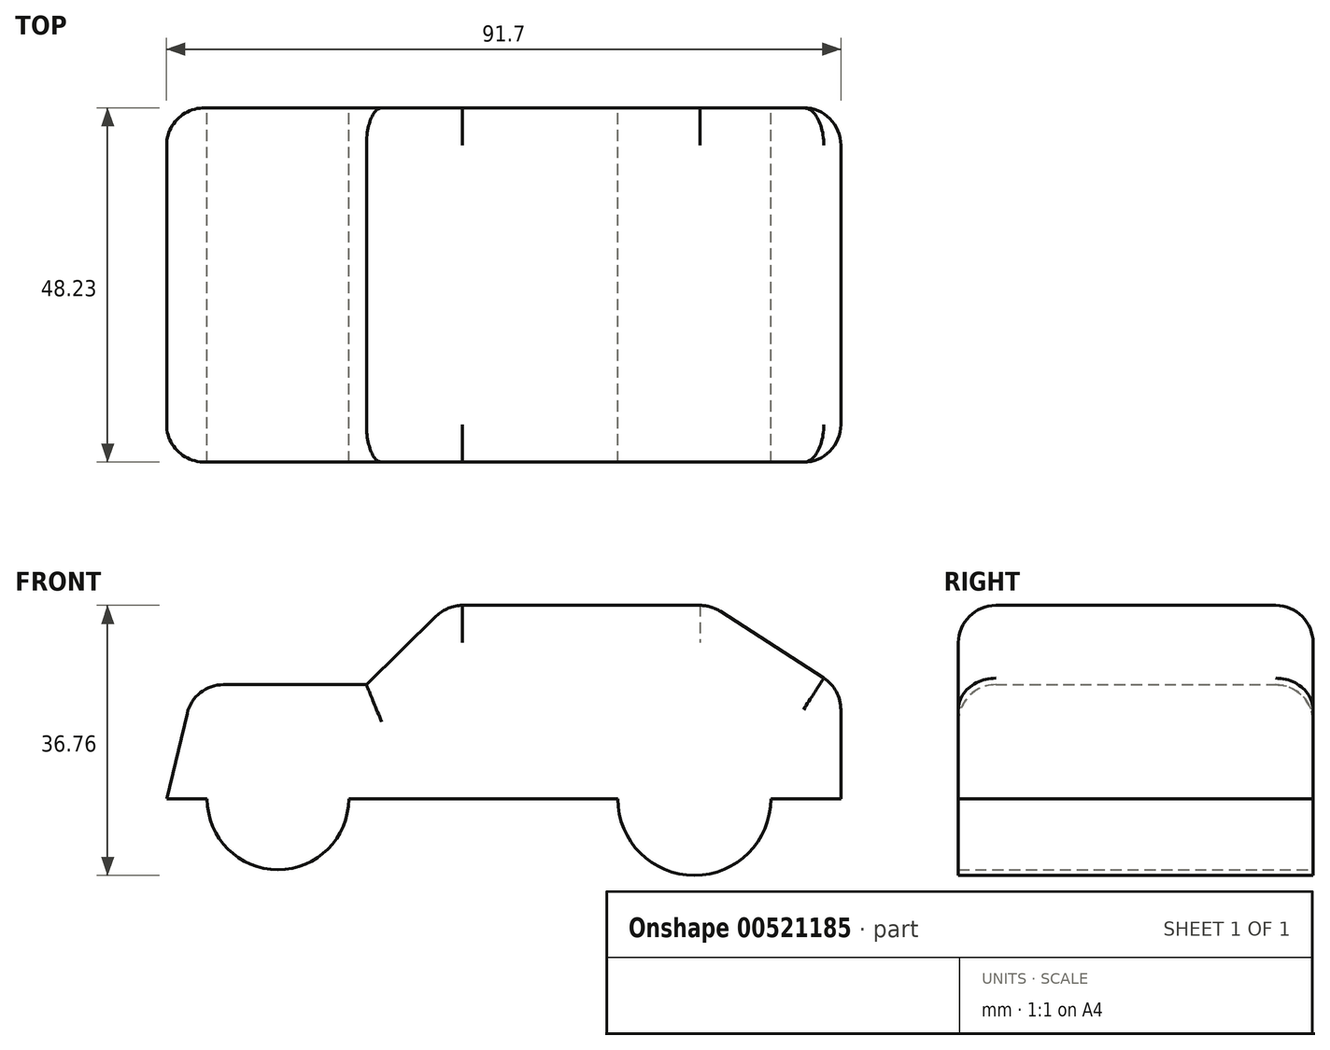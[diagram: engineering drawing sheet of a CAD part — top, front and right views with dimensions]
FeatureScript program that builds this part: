
annotation { "Feature Type Name" : "Feature", "Feature Type Description" : "" }
export const myFeature = defineFeature(function(context is Context, id is Id, definition is map)
    precondition{}
    {
        {
            var Q0;
            Q0=qCreatedBy(makeId("Front.planeOp"),FACE);
            var sketch = newSketch(context, id + "F0", { "sketchPlane" : qUnion([Q0])});
            skLineSegment(sketch, "E0", {"start": v(-48.55, 0) * mm, "end": v(43.15, 0) * mm});
            skLineSegment(sketch, "E1", {"start": v(43.15, 0) * mm, "end": v(43.15, 14.94) * mm});
            skLineSegment(sketch, "E2", {"start": v(43.15, 14.94) * mm, "end": v(25.52, 26.35) * mm});
            skLineSegment(sketch, "E3", {"start": v(25.52, 26.35) * mm, "end": v(-10.37, 26.35) * mm});
            skLineSegment(sketch, "E4", {"start": v(-10.37, 26.35) * mm, "end": v(-21.37, 15.56) * mm});
            skLineSegment(sketch, "E5", {"start": v(-21.37, 15.56) * mm, "end": v(-44.81, 15.56) * mm});
            skLineSegment(sketch, "E6", {"start": v(-44.81, 15.56) * mm, "end": v(-48.55, 0) * mm});
            skCircle(sketch, "E7", {"center": v(-33.4, 0) * mm, "radius": 9.62 * mm});
            skCircle(sketch, "E8", {"center": v(23.24, 0) * mm, "radius": 10.4 * mm});
            skSolve(sketch);
        }
        {
            var Q0;
            Q0 = qSketchRegion(id + "F0", true);
            extrude(context, id + "F1", {"entities" : qUnion([Q0]), "depth" : 25.4 * mm, "offsetDistance" : 25.4 * mm});
        }
        {
            var Q0;
            Q0=makeQuery(id+"F1.opExtrude","CAP_FACE",FACE,{"disambiguationData":[OSD([sQuery(id+"F0.wireOp",EDGE,"E0"),sQuery(id+"F0.wireOp",EDGE,"E1"),sQuery(id+"F0.wireOp",EDGE,"E2"),sQuery(id+"F0.wireOp",EDGE,"E3"),sQuery(id+"F0.wireOp",EDGE,"E4"),sQuery(id+"F0.wireOp",EDGE,"E5"),sQuery(id+"F0.wireOp",EDGE,"E6"),sQuery(id+"F0.wireOp",EDGE,"E7"),sQuery(id+"F0.wireOp",EDGE,"E8")])],"isStart":true});
            extrude(context, id + "F2", {"entities" : qUnion([Q0]), "operationType" : NewBodyOperationType.ADD, "depth" : 22.83 * mm, "offsetDistance" : 25.4 * mm});
        }
        {
            var Q0;
            Q0=makeQuery(id+"F2.opExtrude","CAP_EDGE",EDGE,{"disambiguationData":[OSD([sQuery(id+"F0.wireOp",EDGE,"E3")])],"isStart":false});
            fillet(context, id + "F3", {"entities" : qUnion([Q0]), "radius" : 5.08 * mm, "tangentPropagation" : true, "allowEdgeOverflow" : false});
        }
        {
            var Q0;
            Q0=makeQuery(id+"F2.opExtrude","CAP_EDGE",EDGE,{"disambiguationData":[OSD([sQuery(id+"F0.wireOp",EDGE,"E5")])],"isStart":false});
            fillet(context, id + "F4", {"entities" : qUnion([Q0]), "radius" : 5.08 * mm, "tangentPropagation" : true, "allowEdgeOverflow" : false});
        }
        {
            var Q0;
            Q0=makeQuery(id+"F2.opExtrude","CAP_EDGE",EDGE,{"disambiguationData":[OSD([sQuery(id+"F0.wireOp",EDGE,"E2")])],"isStart":false});
            fillet(context, id + "F5", {"entities" : qUnion([Q0]), "radius" : 5.08 * mm, "tangentPropagation" : true, "allowEdgeOverflow" : false});
        }
        {
            var Q0;
            Q0=makeQuery(id+"F1.opExtrude","CAP_EDGE",EDGE,{"disambiguationData":[OSD([sQuery(id+"F0.wireOp",EDGE,"E2")])],"isStart":false});
            fillet(context, id + "F6", {"entities" : qUnion([Q0]), "radius" : 5.08 * mm, "tangentPropagation" : true, "allowEdgeOverflow" : false});
        }
        {
            var Q0;
            Q0=makeQuery(id+"F1.opExtrude","CAP_EDGE",EDGE,{"disambiguationData":[OSD([sQuery(id+"F0.wireOp",EDGE,"E5")])],"isStart":false});
            fillet(context, id + "F7", {"entities" : qUnion([Q0]), "radius" : 5.08 * mm, "tangentPropagation" : true, "allowEdgeOverflow" : false});
        }
        {
            var Q0;
            {var subQ0=sQuery(id+"F0.wireOp",EDGE,"E4");Q0=makeQuery(id+"F3.opFillet","BLEND_EDGE",EDGE,{"blendedFrom":[makeQuery(id+"F2.opExtrude","CAP_EDGE",EDGE,{"disambiguationData":[OSD([sQuery(id+"F0.wireOp",EDGE,"E3")])],"isStart":false}),makeQuery(id+"F2.boolean.opBoolean","MERGE",FACE,{"derivedFrom":[makeQuery(id+"F1.opExtrude","SWEPT_FACE",FACE,{"disambiguationData":[OSD([subQ0])]}),makeQuery(id+"F2.opExtrude","SWEPT_FACE",FACE,{"disambiguationData":[OSD([subQ0])]})]})],"blendedInto":[makeQuery(id+"F2.boolean.opBoolean","MERGE",FACE,{"derivedFrom":[makeQuery(id+"F1.opExtrude","SWEPT_FACE",FACE,{"disambiguationData":[OSD([subQ0])]}),makeQuery(id+"F2.opExtrude","SWEPT_FACE",FACE,{"disambiguationData":[OSD([subQ0])]})]})]});}
            fillet(context, id + "F8", {"entities" : qUnion([Q0]), "radius" : 5.08 * mm, "tangentPropagation" : true, "allowEdgeOverflow" : false});
        }
        {
            var Q0;
            Q0=makeQuery(id+"F1.opExtrude","CAP_EDGE",EDGE,{"disambiguationData":[OSD([sQuery(id+"F0.wireOp",EDGE,"E6")])],"isStart":false});
            fillet(context, id + "F9", {"entities" : qUnion([Q0]), "radius" : 5.08 * mm, "tangentPropagation" : true, "allowEdgeOverflow" : false});
        }
        {
            var Q0;
            Q0=makeQuery(id+"F1.opExtrude","CAP_EDGE",EDGE,{"disambiguationData":[OSD([sQuery(id+"F0.wireOp",EDGE,"E1")])],"isStart":false});
            fillet(context, id + "F10", {"entities" : qUnion([Q0]), "radius" : 5.08 * mm, "tangentPropagation" : true, "allowEdgeOverflow" : false});
        }
    });
